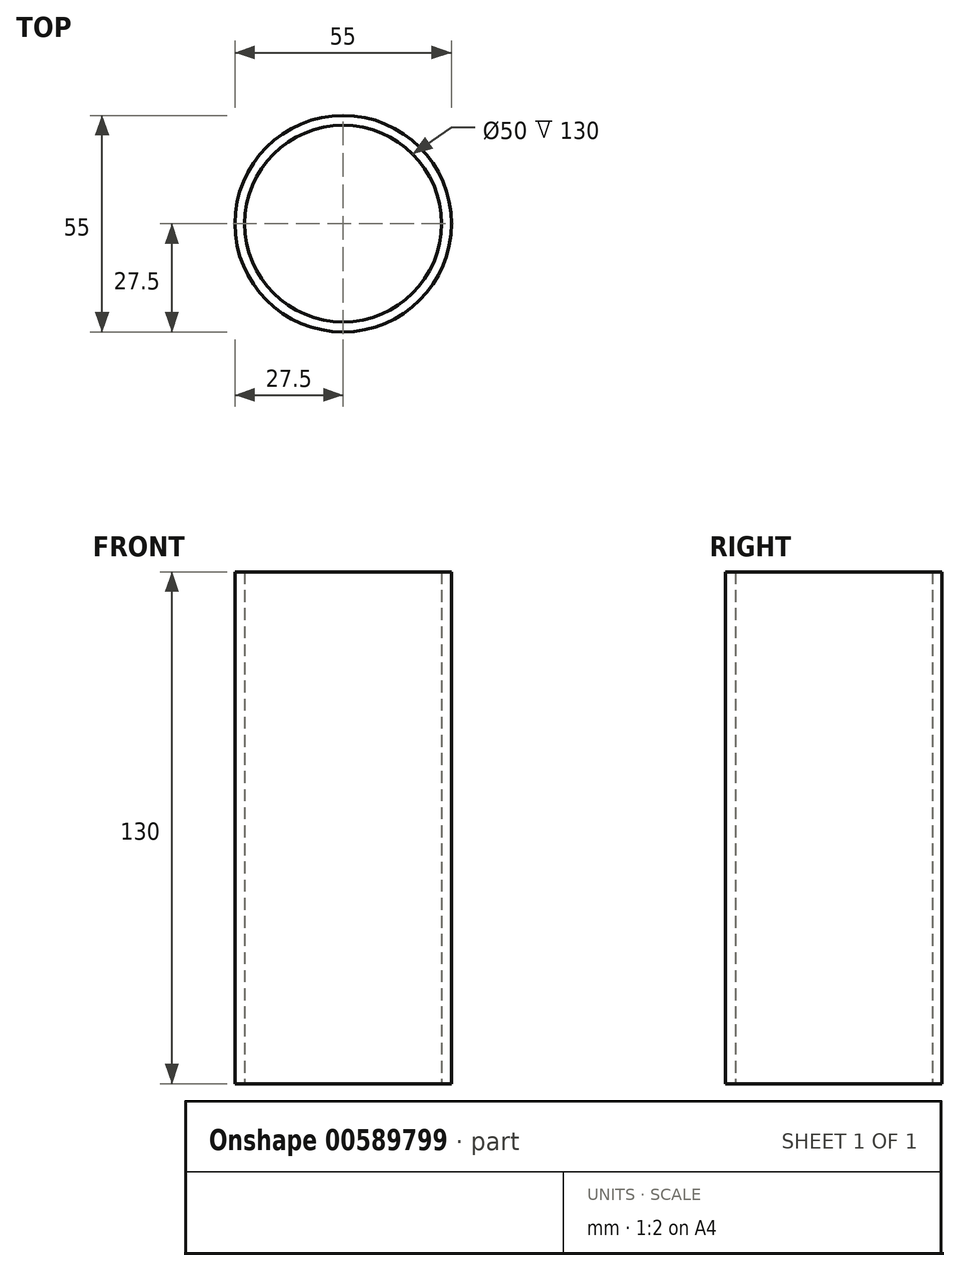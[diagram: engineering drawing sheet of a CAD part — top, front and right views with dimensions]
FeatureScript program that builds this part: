
annotation { "Feature Type Name" : "Feature", "Feature Type Description" : "" }
export const myFeature = defineFeature(function(context is Context, id is Id, definition is map)
    precondition{}
    {
        {
            var Q0;
            Q0=qCreatedBy(makeId("Right.planeOp"),FACE);
            var sketch = newSketch(context, id + "F0", { "sketchPlane" : qUnion([Q0])});
            skLineSegment(sketch, "E0", {"start": v(0, 0) * mm, "end": v(0, 130) * mm});
            skSolve(sketch);
        }
        {
            var Q0;
            Q0=qCreatedBy(makeId("Top.planeOp"),FACE);
            var sketch = newSketch(context, id + "F1", { "sketchPlane" : qUnion([Q0])});
            skCircle(sketch, "E1", {"center": v(0, 0) * mm, "radius": 27.5 * mm});
            skCircle(sketch, "E2", {"center": v(0, 0) * mm, "radius": 25 * mm});
            skLineSegment(sketch, "E3", {"start": v(0, 27.5) * mm, "end": v(0, -27.5) * mm});
            skLineSegment(sketch, "E4", {"start": v(27.5, 0) * mm, "end": v(-27.5, 0) * mm});
            skLineSegment(sketch, "E5", {"start": v(0, 0) * mm, "end": v(26.97, -5.36) * mm});
            skLineSegment(sketch, "E6", {"start": v(0, 0) * mm, "end": v(25.4, -10.52) * mm});
            skLineSegment(sketch, "E7", {"start": v(0, 0) * mm, "end": v(19.45, -19.45) * mm});
            skLineSegment(sketch, "E8", {"start": v(0, 0) * mm, "end": v(10.52, -25.4) * mm});
            skLineSegment(sketch, "E9", {"start": v(0, 0) * mm, "end": v(22.87, -15.28) * mm});
            skLineSegment(sketch, "E10", {"start": v(0, 0) * mm, "end": v(15.28, -22.87) * mm});
            skLineSegment(sketch, "E11", {"start": v(0, 0) * mm, "end": v(5.36, -26.97) * mm});
            skLineSegment(sketch, "E12", {"start": v(0, 0) * mm, "end": v(-5.36, -26.97) * mm});
            skLineSegment(sketch, "E13", {"start": v(0, 0) * mm, "end": v(-10.52, -25.4) * mm});
            skLineSegment(sketch, "E14", {"start": v(0, 0) * mm, "end": v(-15.28, -22.87) * mm});
            skLineSegment(sketch, "E15", {"start": v(0, 0) * mm, "end": v(-19.45, -19.45) * mm});
            skLineSegment(sketch, "E16", {"start": v(0, 0) * mm, "end": v(-22.87, -15.28) * mm});
            skLineSegment(sketch, "E17", {"start": v(0, 0) * mm, "end": v(-25.4, -10.52) * mm});
            skLineSegment(sketch, "E18", {"start": v(0, 0) * mm, "end": v(-27.28, -5.43) * mm});
            skLineSegment(sketch, "E19", {"start": v(0, 0) * mm, "end": v(-26.97, 5.36) * mm});
            skLineSegment(sketch, "E20", {"start": v(0, 0) * mm, "end": v(-25.4, 10.52) * mm});
            skLineSegment(sketch, "E21", {"start": v(0, 0) * mm, "end": v(-22.87, 15.28) * mm});
            skLineSegment(sketch, "E22", {"start": v(0, 0) * mm, "end": v(-19.45, 19.45) * mm});
            skLineSegment(sketch, "E23", {"start": v(0, 0) * mm, "end": v(-15.28, 22.87) * mm});
            skLineSegment(sketch, "E24", {"start": v(0, 0) * mm, "end": v(-10.52, 25.4) * mm});
            skLineSegment(sketch, "E25", {"start": v(0, 0) * mm, "end": v(-5.36, 26.97) * mm});
            skLineSegment(sketch, "E26", {"start": v(0, 0) * mm, "end": v(26.97, 5.36) * mm});
            skLineSegment(sketch, "E27", {"start": v(0, 0) * mm, "end": v(25.4, 10.52) * mm});
            skLineSegment(sketch, "E28", {"start": v(0, 0) * mm, "end": v(19.45, 19.45) * mm});
            skLineSegment(sketch, "E29", {"start": v(0, 0) * mm, "end": v(15.28, 22.87) * mm});
            skLineSegment(sketch, "E30", {"start": v(0, 0) * mm, "end": v(10.52, 25.4) * mm});
            skLineSegment(sketch, "E31", {"start": v(0, 0) * mm, "end": v(5.36, 26.97) * mm});
            skLineSegment(sketch, "E32", {"start": v(0, 0) * mm, "end": v(22.87, 15.28) * mm});
            skSolve(sketch);
        }
        {
            var Q0;
            Q0 = qSketchRegion(id + "F1", true);
            extrude(context, id + "F2", {"entities" : qUnion([Q0]), "depth" : 3.6 * mm, "offsetDistance" : 25 * mm});
        }
        {
            var Q0;
            {var subQ0=sQuery(id+"F1.wireOp",EDGE,"E4");var subQ1=sQuery(id+"F1.wireOp",EDGE,"E1");var subQ2=makeQuery(id+"F1.imprint","INTERSECT",VERTEX,{"disambiguationData":[OD(0.0)],"derivedFrom":[subQ1,subQ0]});Q0=makeQuery(id+"F1.imprint","IMPRINT",FACE,{"disambiguationData":[TD([[makeQuery(id+"F1.imprint","IMPRINT",EDGE,{"disambiguationData":[TD([[subQ2,1.0]])],"derivedFrom":subQ1}),1.0]])]});}
            var Q1;
            {var subQ0=sQuery(id+"F1.wireOp",EDGE,"E7");var subQ1=sQuery(id+"F1.wireOp",EDGE,"E1");var subQ2=makeQuery(id+"F1.imprint","INTERSECT",VERTEX,{"derivedFrom":[subQ1,subQ0]});Q1=makeQuery(id+"F1.imprint","IMPRINT",FACE,{"disambiguationData":[TD([[makeQuery(id+"F1.imprint","IMPRINT",EDGE,{"disambiguationData":[TD([[subQ2,-1.0]])],"derivedFrom":subQ1}),1.0]])]});}
            var Q2;
            {var subQ0=sQuery(id+"F1.wireOp",EDGE,"E8");var subQ1=sQuery(id+"F1.wireOp",EDGE,"E1");var subQ2=makeQuery(id+"F1.imprint","INTERSECT",VERTEX,{"derivedFrom":[subQ1,subQ0]});Q2=makeQuery(id+"F1.imprint","IMPRINT",FACE,{"disambiguationData":[TD([[makeQuery(id+"F1.imprint","IMPRINT",EDGE,{"disambiguationData":[TD([[subQ2,1.0]])],"derivedFrom":subQ1}),1.0]])]});}
            var Q3;
            {var subQ0=sQuery(id+"F1.wireOp",EDGE,"E27");var subQ1=sQuery(id+"F1.wireOp",EDGE,"E1");var subQ2=makeQuery(id+"F1.imprint","INTERSECT",VERTEX,{"derivedFrom":[subQ1,subQ0]});Q3=makeQuery(id+"F1.imprint","IMPRINT",FACE,{"disambiguationData":[TD([[makeQuery(id+"F1.imprint","IMPRINT",EDGE,{"disambiguationData":[TD([[subQ2,-1.0]])],"derivedFrom":subQ1}),1.0]])]});}
            var Q4;
            {var subQ0=sQuery(id+"F1.wireOp",EDGE,"E29");var subQ1=sQuery(id+"F1.wireOp",EDGE,"E1");var subQ2=makeQuery(id+"F1.imprint","INTERSECT",VERTEX,{"derivedFrom":[subQ1,subQ0]});Q4=makeQuery(id+"F1.imprint","IMPRINT",FACE,{"disambiguationData":[TD([[makeQuery(id+"F1.imprint","IMPRINT",EDGE,{"disambiguationData":[TD([[subQ2,-1.0]])],"derivedFrom":subQ1}),1.0]])]});}
            var Q5;
            {var subQ0=sQuery(id+"F1.wireOp",EDGE,"E3");var subQ1=sQuery(id+"F1.wireOp",EDGE,"E1");var subQ2=makeQuery(id+"F1.imprint","INTERSECT",VERTEX,{"disambiguationData":[OD(0.0)],"derivedFrom":[subQ1,subQ0]});Q5=makeQuery(id+"F1.imprint","IMPRINT",FACE,{"disambiguationData":[TD([[makeQuery(id+"F1.imprint","IMPRINT",EDGE,{"disambiguationData":[TD([[subQ2,-1.0]])],"derivedFrom":subQ1}),1.0]])]});}
            var Q6;
            {var subQ0=sQuery(id+"F1.wireOp",EDGE,"E12");var subQ1=sQuery(id+"F1.wireOp",EDGE,"E1");var subQ2=makeQuery(id+"F1.imprint","INTERSECT",VERTEX,{"derivedFrom":[subQ1,subQ0]});Q6=makeQuery(id+"F1.imprint","IMPRINT",FACE,{"disambiguationData":[TD([[makeQuery(id+"F1.imprint","IMPRINT",EDGE,{"disambiguationData":[TD([[subQ2,1.0]])],"derivedFrom":subQ1}),1.0]])]});}
            var Q7;
            {var subQ0=sQuery(id+"F1.wireOp",EDGE,"E22");var subQ1=sQuery(id+"F1.wireOp",EDGE,"E1");var subQ2=makeQuery(id+"F1.imprint","INTERSECT",VERTEX,{"derivedFrom":[subQ1,subQ0]});Q7=makeQuery(id+"F1.imprint","IMPRINT",FACE,{"disambiguationData":[TD([[makeQuery(id+"F1.imprint","IMPRINT",EDGE,{"disambiguationData":[TD([[subQ2,1.0]])],"derivedFrom":subQ1}),1.0]])]});}
            var Q8;
            {var subQ0=sQuery(id+"F1.wireOp",EDGE,"E19");var subQ1=sQuery(id+"F1.wireOp",EDGE,"E1");var subQ2=makeQuery(id+"F1.imprint","INTERSECT",VERTEX,{"derivedFrom":[subQ1,subQ0]});Q8=makeQuery(id+"F1.imprint","IMPRINT",FACE,{"disambiguationData":[TD([[makeQuery(id+"F1.imprint","IMPRINT",EDGE,{"disambiguationData":[TD([[subQ2,1.0]])],"derivedFrom":subQ1}),1.0]])]});}
            var Q9;
            {var subQ0=sQuery(id+"F1.wireOp",EDGE,"E15");var subQ1=sQuery(id+"F1.wireOp",EDGE,"E1");var subQ2=makeQuery(id+"F1.imprint","INTERSECT",VERTEX,{"derivedFrom":[subQ1,subQ0]});Q9=makeQuery(id+"F1.imprint","IMPRINT",FACE,{"disambiguationData":[TD([[makeQuery(id+"F1.imprint","IMPRINT",EDGE,{"disambiguationData":[TD([[subQ2,1.0]])],"derivedFrom":subQ1}),1.0]])]});}
            var Q10;
            {var subQ0=sQuery(id+"F1.wireOp",EDGE,"E4");var subQ1=sQuery(id+"F1.wireOp",EDGE,"E1");var subQ2=makeQuery(id+"F1.imprint","INTERSECT",VERTEX,{"disambiguationData":[OD(1.0)],"derivedFrom":[subQ1,subQ0]});Q10=makeQuery(id+"F1.imprint","IMPRINT",FACE,{"disambiguationData":[TD([[makeQuery(id+"F1.imprint","IMPRINT",EDGE,{"disambiguationData":[TD([[subQ2,-1.0]])],"derivedFrom":subQ1}),1.0]])]});}
            extrude(context, id + "F3", {"entities" : qUnion([Q0, Q1, Q2, Q3, Q4, Q5, Q6, Q7, Q8, Q9, Q10]), "operationType" : NewBodyOperationType.ADD, "depth" : 130 * mm, "offsetDistance" : 25 * mm});
        }
    });
